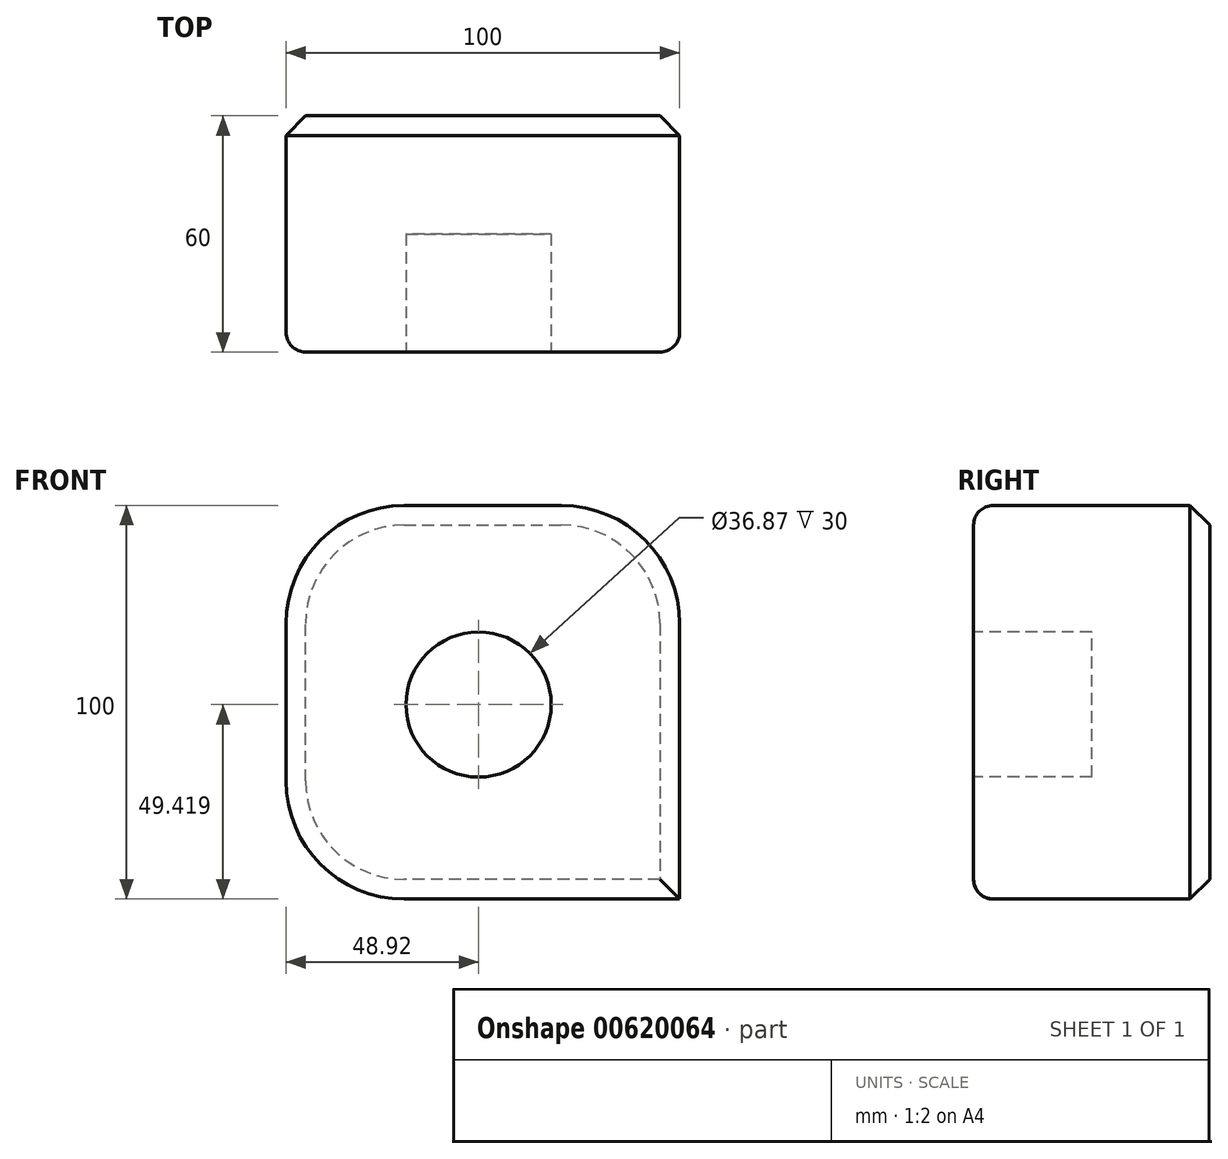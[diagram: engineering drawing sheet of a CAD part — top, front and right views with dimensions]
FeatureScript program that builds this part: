
annotation { "Feature Type Name" : "Feature", "Feature Type Description" : "" }
export const myFeature = defineFeature(function(context is Context, id is Id, definition is map)
    precondition{}
    {
        {
            var Q0;
            Q0=qCreatedBy(makeId("Front.planeOp"),FACE);
            var sketch = newSketch(context, id + "F0", { "sketchPlane" : qUnion([Q0])});
            skLineSegment(sketch, "E0.bottom", {"start": v(-18.92, 76.11) * mm, "end": v(21.08, 76.11) * mm});
            skLineSegment(sketch, "E0.top", {"start": v(-18.92, -23.89) * mm, "end": v(51.08, -23.89) * mm});
            skLineSegment(sketch, "E0.left", {"start": v(-48.92, 46.11) * mm, "end": v(-48.92, 6.11) * mm});
            skLineSegment(sketch, "E0.right", {"start": v(51.08, 46.11) * mm, "end": v(51.08, -23.89) * mm});
            skPoint(sketch, "E1.visualSharp", {"position": v(-48.92, 76.11) * mm});
            skArc(sketch, "E1.filletArc", {"start": v(-18.92, 76.11) * mm, "mid": v(-40.13, 67.33) * mm, "end": v(-48.92, 46.11) * mm});
            skPoint(sketch, "E2.visualSharp", {"position": v(-48.92, -23.89) * mm});
            skArc(sketch, "E2.filletArc", {"start": v(-48.92, 6.11) * mm, "mid": v(-40.13, -15.1) * mm, "end": v(-18.92, -23.89) * mm});
            skPoint(sketch, "E3.visualSharp", {"position": v(51.08, 76.11) * mm});
            skArc(sketch, "E3.filletArc", {"start": v(51.08, 46.11) * mm, "mid": v(42.3, 67.33) * mm, "end": v(21.08, 76.11) * mm});
            skSolve(sketch);
        }
        {
            var Q0;
            Q0 = qSketchRegion(id + "F0", true);
            extrude(context, id + "F1", {"entities" : qUnion([Q0]), "depth" : 60 * mm, "offsetDistance" : 25 * mm});
        }
        {
            var Q0;
            Q0=makeQuery(id+"F1.opExtrude","CAP_FACE",FACE,{"disambiguationData":[OSD([sQuery(id+"F0.wireOp",EDGE,"E0.bottom"),sQuery(id+"F0.wireOp",EDGE,"E0.top"),sQuery(id+"F0.wireOp",EDGE,"E0.left"),sQuery(id+"F0.wireOp",EDGE,"E0.right"),sQuery(id+"F0.wireOp",EDGE,"E1.filletArc"),sQuery(id+"F0.wireOp",EDGE,"E2.filletArc"),sQuery(id+"F0.wireOp",EDGE,"E3.filletArc")])],"isStart":false});
            fillet(context, id + "F2", {"entities" : qUnion([Q0]), "radius" : 5 * mm, "tangentPropagation" : true, "allowEdgeOverflow" : false});
        }
        {
            var Q0;
            Q0=makeQuery(id+"F1.opExtrude","CAP_FACE",FACE,{"disambiguationData":[OSD([sQuery(id+"F0.wireOp",EDGE,"E0.bottom"),sQuery(id+"F0.wireOp",EDGE,"E0.top"),sQuery(id+"F0.wireOp",EDGE,"E0.left"),sQuery(id+"F0.wireOp",EDGE,"E0.right"),sQuery(id+"F0.wireOp",EDGE,"E1.filletArc"),sQuery(id+"F0.wireOp",EDGE,"E2.filletArc"),sQuery(id+"F0.wireOp",EDGE,"E3.filletArc")])],"isStart":true});
            chamfer(context, id + "F3", {"entities" : qUnion([Q0]), "width" : 5 * mm, "tangentPropagation" : true});
        }
        {
            var Q0;
            Q0=makeQuery(id+"F1.opExtrude","CAP_FACE",FACE,{"disambiguationData":[OSD([sQuery(id+"F0.wireOp",EDGE,"E0.bottom"),sQuery(id+"F0.wireOp",EDGE,"E0.top"),sQuery(id+"F0.wireOp",EDGE,"E0.left"),sQuery(id+"F0.wireOp",EDGE,"E0.right"),sQuery(id+"F0.wireOp",EDGE,"E1.filletArc"),sQuery(id+"F0.wireOp",EDGE,"E2.filletArc"),sQuery(id+"F0.wireOp",EDGE,"E3.filletArc")])],"isStart":false});
            var sketch = newSketch(context, id + "F4", { "sketchPlane" : qUnion([Q0])});
            skCircle(sketch, "E4", {"center": v(0, 25.53) * mm, "radius": 18.44 * mm});
            skSolve(sketch);
        }
        {
            var Q0;
            Q0 = qSketchRegion(id + "F4", true);
            extrude(context, id + "F5", {"entities" : qUnion([Q0]), "operationType" : NewBodyOperationType.REMOVE, "oppositeDirection" : true, "depth" : 30 * mm, "offsetDistance" : 25 * mm});
        }
    });
